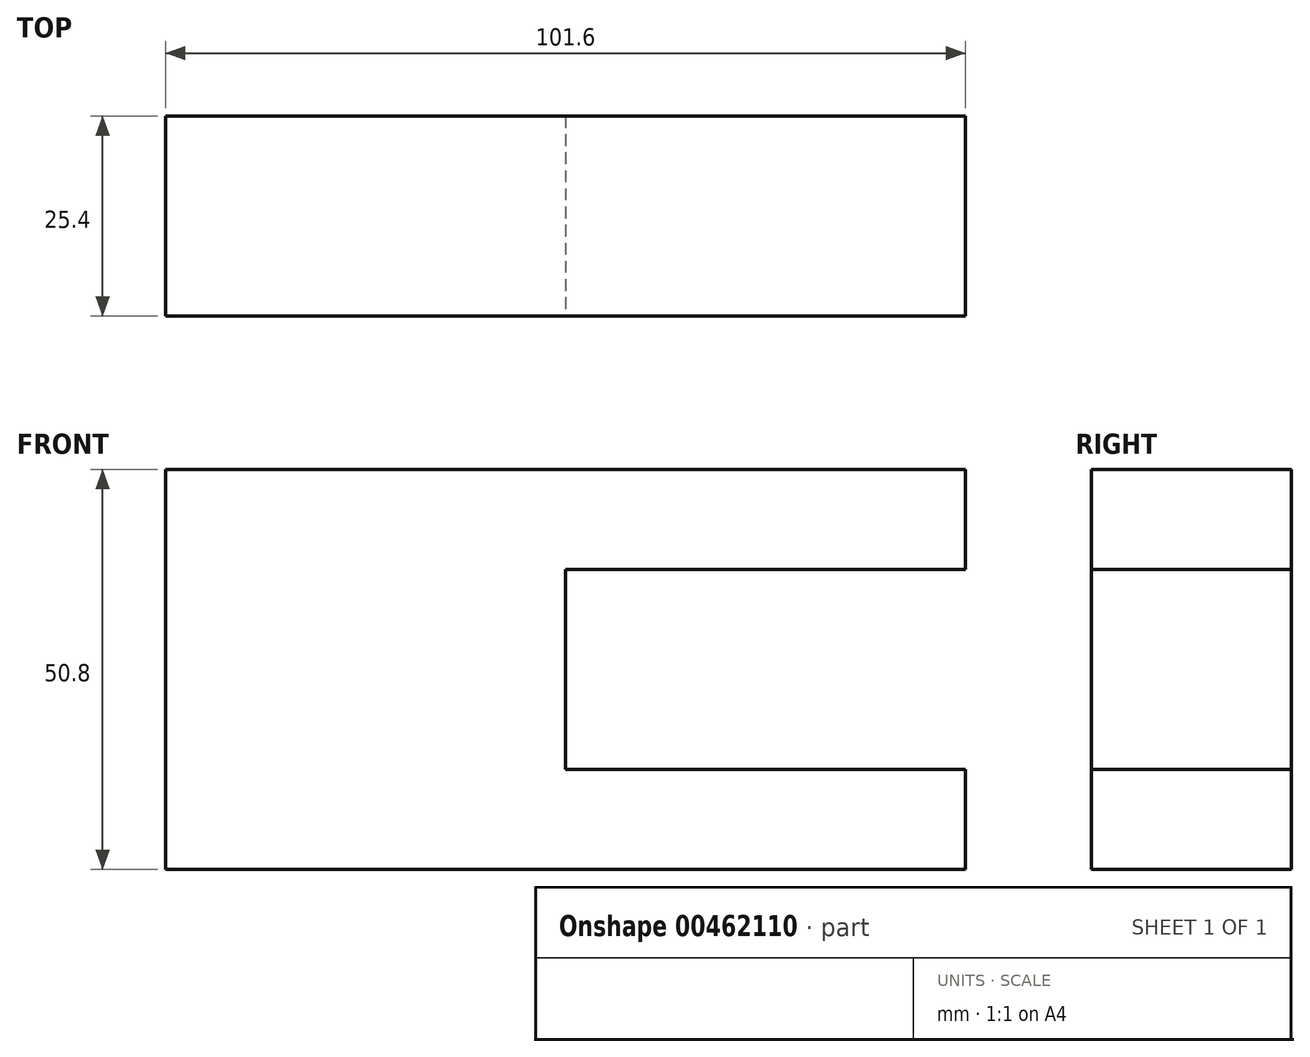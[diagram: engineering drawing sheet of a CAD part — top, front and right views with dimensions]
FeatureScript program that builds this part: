
annotation { "Feature Type Name" : "Feature", "Feature Type Description" : "" }
export const myFeature = defineFeature(function(context is Context, id is Id, definition is map)
    precondition{}
    {
        {
            var Q0;
            Q0=qCreatedBy(makeId("Front.planeOp"),FACE);
            var sketch = newSketch(context, id + "F0", { "sketchPlane" : qUnion([Q0])});
            skLineSegment(sketch, "E0.bottom", {"start": v(50.8, -25.4) * mm, "end": v(-50.8, -25.4) * mm});
            skLineSegment(sketch, "E0.top", {"start": v(50.8, 25.4) * mm, "end": v(-50.8, 25.4) * mm});
            skLineSegment(sketch, "E0.left", {"start": v(50.8, -25.4) * mm, "end": v(50.8, 25.4) * mm});
            skLineSegment(sketch, "E0.right", {"start": v(-50.8, -25.4) * mm, "end": v(-50.8, 25.4) * mm});
            skPoint(sketch, "E0.middle", {"position": v(0, 0) * mm});
            skSolve(sketch);
        }
        {
            var Q0;
            Q0 = qSketchRegion(id + "F0", true);
            extrude(context, id + "F1", {"entities" : qUnion([Q0]), "depth" : 25.4 * mm});
        }
        {
            var Q0;
            Q0=makeQuery(id+"F1.opExtrude","CAP_FACE",FACE,{"disambiguationData":[OSD([sQuery(id+"F0.wireOp",EDGE,"E0.bottom"),sQuery(id+"F0.wireOp",EDGE,"E0.top"),sQuery(id+"F0.wireOp",EDGE,"E0.left"),sQuery(id+"F0.wireOp",EDGE,"E0.right")])],"isStart":false});
            var sketch = newSketch(context, id + "F2", { "sketchPlane" : qUnion([Q0])});
            skLineSegment(sketch, "E1.bottom", {"start": v(50.8, 25.4) * mm, "end": v(42.41, 25.4) * mm});
            skLineSegment(sketch, "E1.top", {"start": v(50.8, 25.4) * mm, "end": v(42.41, 25.4) * mm});
            skLineSegment(sketch, "E1.left", {"start": v(50.8, 25.4) * mm, "end": v(50.8, 25.4) * mm});
            skLineSegment(sketch, "E1.right", {"start": v(42.41, 25.4) * mm, "end": v(42.41, 25.4) * mm});
            skLineSegment(sketch, "E2.bottom", {"start": v(50.8, 12.7) * mm, "end": v(0, 12.7) * mm});
            skLineSegment(sketch, "E2.top", {"start": v(50.8, -12.7) * mm, "end": v(0, -12.7) * mm});
            skLineSegment(sketch, "E2.left", {"start": v(50.8, 12.7) * mm, "end": v(50.8, -12.7) * mm});
            skLineSegment(sketch, "E2.right", {"start": v(0, 12.7) * mm, "end": v(0, -12.7) * mm});
            skSolve(sketch);
        }
        {
            var Q0;
            Q0 = qSketchRegion(id + "F2", true);
            extrude(context, id + "F3", {"entities" : qUnion([Q0]), "operationType" : NewBodyOperationType.REMOVE, "oppositeDirection" : true, "depth" : 25.4 * mm});
        }
    });
